# Revit family: 53_OE619B-400SA
name_source: partatom
category: Equipos especializados
units: mm (PartAtom-declared; Revit-internal decimal feet)

## family parameters
Compartido = No
Corte con vacíos al cargar = No
Cota de conector redondo = Diámetro de uso
Punto de cálculo de habitación = No
Se basa en plano de trabajo = No
Siempre vertical = Sí
Tipo de pieza = Normal

## types (1)
- OE619B-400SA
    Aislación = Triple Capa
    Alto = 60 cm
    Ancho = 60 cm
    Aprobaciones = CE/GS/CB/SAA
    Asa Puerta de Horno = Iron, Gray
    Asa Tope = Tapa Asa
    Color Logo = Logo
    Convección = Forzada
    Creado por = Unibim
    Cuerpo Horno = Steel, Galvanized
    Descripción = Horno eléctrico empotrable, marca Vatti, modelo OE619B-400SA
    Elevación por defecto = 0 cm
    Especificación Técnica = Horno eléctrico empotrable, marca Vatti, modelo OE619B-400SA
    Fabricante = Vatti
    Facilidad de Uso = 4 programas de cocción
    Fondo = 51 cm
    Grill = Sí
    Instalación = Empotrado
    Luz Interior = Sí
    Modelo = OE619B-400SA
    Modo de Control = Con Autoapagado
    Panel Control = Panel Negro
    Panel Control Cubierta = Panel Vidrio
    Paneles = Vidrio - Acero Inox
    Perilla Exterior = Acero Inox
    Perilla Interior = Perilla Negro
    Peso = 28,5 Kg
    Potencia = 2035 W
    Puerta Interior = Interior Negro
    Puerta Negro = Panel Negro
    Puerta Vidiro = Panel Vidrio
    Rieles para bandejas = Multiposición- Extraíbles
    Sello puerta = Perimetral 100%
    Tamaño del corte en superficie = 600 x 600
    Tamaño del producto = 600 x 600 x 515
    Temperatura Máxima = 250° C
    Temporizador = Sí
    Termostato con luz indicadora = Sí
    Timer = con Autoapagado
    Tirador de puerta = Acero Inox
    URL = www.vatti.cl
    Vidrio interior desmontable = Easy Clean
    Voltage / Frecuencia = 220 V
    Volumen interior = 61 Litros

## geometry (parser evidence)
native form markers: Sweep x3
no freeform markers — native parametric forms only
